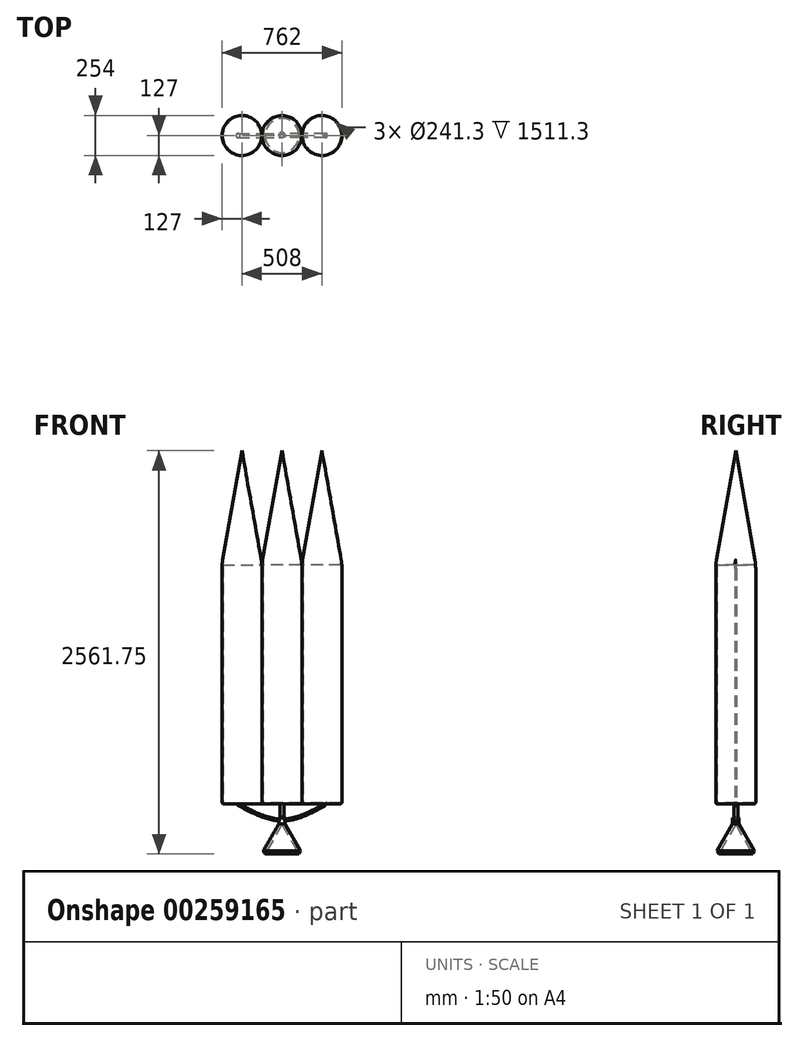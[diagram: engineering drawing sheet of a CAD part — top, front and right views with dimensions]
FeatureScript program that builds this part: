
annotation { "Feature Type Name" : "Feature", "Feature Type Description" : "" }
export const myFeature = defineFeature(function(context is Context, id is Id, definition is map)
    precondition{}
    {
        {
            var Q0;
            Q0=qCreatedBy(makeId("Top.planeOp"),FACE);
            var sketch = newSketch(context, id + "F0", { "sketchPlane" : qUnion([Q0])});
            skCircle(sketch, "E0", {"center": v(0, 0) * mm, "radius": 127 * mm});
            skCircle(sketch, "E1", {"center": v(-127, 0) * mm, "radius": 127 * mm});
            skCircle(sketch, "E2", {"center": v(-254, 0) * mm, "radius": 127 * mm});
            skCircle(sketch, "E3", {"center": v(127, 0) * mm, "radius": 127 * mm});
            skCircle(sketch, "E4", {"center": v(254, 0) * mm, "radius": 127 * mm});
            skLineSegment(sketch, "E5.bottom", {"start": v(-276, 5.08) * mm, "end": v(273.28, 5.08) * mm});
            skLineSegment(sketch, "E5.top", {"start": v(-276, -5.08) * mm, "end": v(273.28, -5.08) * mm});
            skLineSegment(sketch, "E5.left", {"start": v(-276, 5.08) * mm, "end": v(-276, -5.08) * mm});
            skLineSegment(sketch, "E5.right", {"start": v(273.28, 5.08) * mm, "end": v(273.28, -5.08) * mm});
            skSolve(sketch);
        }
        {
            var Q0;
            {var subQ0=sQuery(id+"F0.wireOp",EDGE,"E3");var subQ1=sQuery(id+"F0.wireOp",EDGE,"E0");var subQ2=makeQuery(id+"F0.imprint","INTERSECT",VERTEX,{"disambiguationData":[OD(0.0)],"derivedFrom":[subQ1,subQ0]});Q0=makeQuery(id+"F0.imprint","IMPRINT",FACE,{"disambiguationData":[TD([[makeQuery(id+"F0.imprint","IMPRINT",EDGE,{"disambiguationData":[TD([[subQ2,1.0]])],"derivedFrom":subQ1}),1.0]])]});}
            var Q1;
            {var subQ0=sQuery(id+"F0.wireOp",EDGE,"E3");var subQ1=sQuery(id+"F0.wireOp",EDGE,"E0");var subQ2=makeQuery(id+"F0.imprint","INTERSECT",VERTEX,{"disambiguationData":[OD(0.0)],"derivedFrom":[subQ1,subQ0]});Q1=makeQuery(id+"F0.imprint","IMPRINT",FACE,{"disambiguationData":[TD([[makeQuery(id+"F0.imprint","IMPRINT",EDGE,{"disambiguationData":[TD([[subQ2,-1.0]])],"derivedFrom":subQ1}),1.0]])]});}
            var Q2;
            {var subQ0=sQuery(id+"F0.wireOp",EDGE,"E1");var subQ1=sQuery(id+"F0.wireOp",EDGE,"E0");var subQ2=makeQuery(id+"F0.imprint","INTERSECT",VERTEX,{"disambiguationData":[OD(0.0)],"derivedFrom":[subQ1,subQ0]});Q2=makeQuery(id+"F0.imprint","IMPRINT",FACE,{"disambiguationData":[TD([[makeQuery(id+"F0.imprint","IMPRINT",EDGE,{"disambiguationData":[TD([[subQ2,-1.0]])],"derivedFrom":subQ1}),1.0]])]});}
            var Q3;
            {var subQ0=sQuery(id+"F0.wireOp",EDGE,"E1");var subQ1=sQuery(id+"F0.wireOp",EDGE,"E0");var subQ2=makeQuery(id+"F0.imprint","INTERSECT",VERTEX,{"disambiguationData":[OD(1.0)],"derivedFrom":[subQ1,subQ0]});Q3=makeQuery(id+"F0.imprint","IMPRINT",FACE,{"disambiguationData":[TD([[makeQuery(id+"F0.imprint","IMPRINT",EDGE,{"disambiguationData":[TD([[subQ2,1.0]])],"derivedFrom":subQ1}),1.0]])]});}
            var Q4;
            {var subQ0=sQuery(id+"F0.wireOp",EDGE,"E1");var subQ1=sQuery(id+"F0.wireOp",EDGE,"E0");var subQ2=makeQuery(id+"F0.imprint","INTERSECT",VERTEX,{"disambiguationData":[OD(1.0)],"derivedFrom":[subQ1,subQ0]});Q4=makeQuery(id+"F0.imprint","IMPRINT",FACE,{"disambiguationData":[TD([[makeQuery(id+"F0.imprint","IMPRINT",EDGE,{"disambiguationData":[TD([[subQ2,-1.0]])],"derivedFrom":subQ1}),1.0]])]});}
            var Q5;
            {var subQ0=sQuery(id+"F0.wireOp",EDGE,"E3");var subQ1=sQuery(id+"F0.wireOp",EDGE,"E0");var subQ2=makeQuery(id+"F0.imprint","INTERSECT",VERTEX,{"disambiguationData":[OD(1.0)],"derivedFrom":[subQ1,subQ0]});Q5=makeQuery(id+"F0.imprint","IMPRINT",FACE,{"disambiguationData":[TD([[makeQuery(id+"F0.imprint","IMPRINT",EDGE,{"disambiguationData":[TD([[subQ2,-1.0]])],"derivedFrom":subQ1}),1.0]])]});}
            var Q6;
            {var subQ0=sQuery(id+"F0.wireOp",EDGE,"E5.left");Q6=makeQuery(id+"F0.imprint","IMPRINT",FACE,{"disambiguationData":[TD([[makeQuery(id+"F0.imprint","IMPRINT",EDGE,{"derivedFrom":subQ0}),-1.0]])]});}
            var Q7;
            {var subQ0=sQuery(id+"F0.wireOp",EDGE,"E2");var subQ1=sQuery(id+"F0.wireOp",EDGE,"E1");var subQ2=makeQuery(id+"F0.imprint","INTERSECT",VERTEX,{"disambiguationData":[OD(0.0)],"derivedFrom":[subQ1,subQ0]});Q7=makeQuery(id+"F0.imprint","IMPRINT",FACE,{"disambiguationData":[TD([[makeQuery(id+"F0.imprint","IMPRINT",EDGE,{"disambiguationData":[TD([[subQ2,-1.0]])],"derivedFrom":subQ1}),1.0]])]});}
            var Q8;
            {var subQ0=sQuery(id+"F0.wireOp",EDGE,"E2");var subQ1=sQuery(id+"F0.wireOp",EDGE,"E1");var subQ2=makeQuery(id+"F0.imprint","INTERSECT",VERTEX,{"disambiguationData":[OD(1.0)],"derivedFrom":[subQ1,subQ0]});Q8=makeQuery(id+"F0.imprint","IMPRINT",FACE,{"disambiguationData":[TD([[makeQuery(id+"F0.imprint","IMPRINT",EDGE,{"disambiguationData":[TD([[subQ2,1.0]])],"derivedFrom":subQ1}),1.0]])]});}
            var Q9;
            {var subQ8=sQuery(id+"F0.wireOp",EDGE,"E5.right");Q9=makeQuery(id+"F0.imprint","IMPRINT",FACE,{"disambiguationData":[TD([[makeQuery(id+"F0.imprint","IMPRINT",EDGE,{"derivedFrom":subQ8}),1.0]])]});}
            var Q10;
            {var subQ0=sQuery(id+"F0.wireOp",EDGE,"E4");var subQ1=sQuery(id+"F0.wireOp",EDGE,"E3");var subQ2=makeQuery(id+"F0.imprint","INTERSECT",VERTEX,{"disambiguationData":[OD(0.0)],"derivedFrom":[subQ1,subQ0]});Q10=makeQuery(id+"F0.imprint","IMPRINT",FACE,{"disambiguationData":[TD([[makeQuery(id+"F0.imprint","IMPRINT",EDGE,{"disambiguationData":[TD([[subQ2,1.0]])],"derivedFrom":subQ1}),1.0]])]});}
            var Q11;
            {var subQ0=sQuery(id+"F0.wireOp",EDGE,"E4");var subQ1=sQuery(id+"F0.wireOp",EDGE,"E3");var subQ2=makeQuery(id+"F0.imprint","INTERSECT",VERTEX,{"disambiguationData":[OD(1.0)],"derivedFrom":[subQ1,subQ0]});Q11=makeQuery(id+"F0.imprint","IMPRINT",FACE,{"disambiguationData":[TD([[makeQuery(id+"F0.imprint","IMPRINT",EDGE,{"disambiguationData":[TD([[subQ2,-1.0]])],"derivedFrom":subQ1}),1.0]])]});}
            var Q12;
            {var subQ0=sQuery(id+"F0.wireOp",EDGE,"E5.bottom");var subQ1=sQuery(id+"F0.wireOp",EDGE,"E1");var subQ2=makeQuery(id+"F0.imprint","INTERSECT",VERTEX,{"disambiguationData":[OD(1.0)],"derivedFrom":[subQ1,subQ0]});Q12=makeQuery(id+"F0.imprint","IMPRINT",FACE,{"disambiguationData":[TD([[makeQuery(id+"F0.imprint","IMPRINT",EDGE,{"disambiguationData":[TD([[subQ2,-1.0]])],"derivedFrom":subQ1}),1.0]])]});}
            var Q13;
            {var subQ4=sQuery(id+"F0.wireOp",EDGE,"E5.bottom");var subQ6=sQuery(id+"F0.wireOp",EDGE,"E0");var subQ7=makeQuery(id+"F0.imprint","INTERSECT",VERTEX,{"disambiguationData":[OD(1.0)],"derivedFrom":[subQ6,subQ4]});Q13=makeQuery(id+"F0.imprint","IMPRINT",FACE,{"disambiguationData":[TD([[makeQuery(id+"F0.imprint","IMPRINT",EDGE,{"disambiguationData":[TD([[subQ7,-1.0]])],"derivedFrom":subQ6}),1.0]])]});}
            var Q14;
            {var subQ5=sQuery(id+"F0.wireOp",EDGE,"E5.left");Q14=makeQuery(id+"F0.imprint","IMPRINT",FACE,{"disambiguationData":[TD([[makeQuery(id+"F0.imprint","IMPRINT",EDGE,{"derivedFrom":subQ5}),1.0]])]});}
            var Q15;
            {var subQ4=sQuery(id+"F0.wireOp",EDGE,"E0");var subQ6=sQuery(id+"F0.wireOp",EDGE,"E5.bottom");var subQ8=makeQuery(id+"F0.imprint","INTERSECT",VERTEX,{"disambiguationData":[OD(0.0)],"derivedFrom":[subQ4,subQ6]});Q15=makeQuery(id+"F0.imprint","IMPRINT",FACE,{"disambiguationData":[TD([[makeQuery(id+"F0.imprint","IMPRINT",EDGE,{"disambiguationData":[TD([[subQ8,1.0]])],"derivedFrom":subQ4}),1.0]])]});}
            var Q16;
            {var subQ0=sQuery(id+"F0.wireOp",EDGE,"E5.bottom");var subQ1=sQuery(id+"F0.wireOp",EDGE,"E3");var subQ2=makeQuery(id+"F0.imprint","INTERSECT",VERTEX,{"disambiguationData":[OD(0.0)],"derivedFrom":[subQ1,subQ0]});Q16=makeQuery(id+"F0.imprint","IMPRINT",FACE,{"disambiguationData":[TD([[makeQuery(id+"F0.imprint","IMPRINT",EDGE,{"disambiguationData":[TD([[subQ2,1.0]])],"derivedFrom":subQ1}),1.0]])]});}
            var Q17;
            {var subQ5=sQuery(id+"F0.wireOp",EDGE,"E5.right");Q17=makeQuery(id+"F0.imprint","IMPRINT",FACE,{"disambiguationData":[TD([[makeQuery(id+"F0.imprint","IMPRINT",EDGE,{"derivedFrom":subQ5}),-1.0]])]});}
            var Q18;
            {var subQ0=sQuery(id+"F0.wireOp",EDGE,"E5.bottom");var subQ1=sQuery(id+"F0.wireOp",EDGE,"E0");var subQ2=makeQuery(id+"F0.imprint","INTERSECT",VERTEX,{"disambiguationData":[OD(0.0)],"derivedFrom":[subQ1,subQ0]});Q18=makeQuery(id+"F0.imprint","IMPRINT",FACE,{"disambiguationData":[TD([[makeQuery(id+"F0.imprint","IMPRINT",EDGE,{"disambiguationData":[TD([[subQ2,1.0]])],"derivedFrom":subQ1}),-1.0]])]});}
            var Q19;
            {var subQ0=sQuery(id+"F0.wireOp",EDGE,"E4");var subQ1=sQuery(id+"F0.wireOp",EDGE,"E0");var subQ2=makeQuery(id+"F0.imprint","INTERSECT",VERTEX,{"derivedFrom":[subQ1,subQ0]});Q19=makeQuery(id+"F0.imprint","IMPRINT",FACE,{"disambiguationData":[TD([[makeQuery(id+"F0.imprint","IMPRINT",EDGE,{"disambiguationData":[TD([[subQ2,1.0]])],"derivedFrom":subQ1}),-1.0]])]});}
            var Q20;
            {var subQ0=sQuery(id+"F0.wireOp",EDGE,"E5.bottom");var subQ1=sQuery(id+"F0.wireOp",EDGE,"E0");var subQ2=makeQuery(id+"F0.imprint","INTERSECT",VERTEX,{"disambiguationData":[OD(1.0)],"derivedFrom":[subQ1,subQ0]});Q20=makeQuery(id+"F0.imprint","IMPRINT",FACE,{"disambiguationData":[TD([[makeQuery(id+"F0.imprint","IMPRINT",EDGE,{"disambiguationData":[TD([[subQ2,-1.0]])],"derivedFrom":subQ1}),-1.0]])]});}
            var Q21;
            {var subQ0=sQuery(id+"F0.wireOp",EDGE,"E2");var subQ1=sQuery(id+"F0.wireOp",EDGE,"E0");var subQ2=makeQuery(id+"F0.imprint","INTERSECT",VERTEX,{"derivedFrom":[subQ1,subQ0]});Q21=makeQuery(id+"F0.imprint","IMPRINT",FACE,{"disambiguationData":[TD([[makeQuery(id+"F0.imprint","IMPRINT",EDGE,{"disambiguationData":[TD([[subQ2,-1.0]])],"derivedFrom":subQ1}),-1.0]])]});}
            var Q22;
            {var subQ0=sQuery(id+"F0.wireOp",EDGE,"E3");var subQ1=sQuery(id+"F0.wireOp",EDGE,"E1");var subQ2=makeQuery(id+"F0.imprint","INTERSECT",VERTEX,{"derivedFrom":[subQ1,subQ0]});Q22=makeQuery(id+"F0.imprint","IMPRINT",FACE,{"disambiguationData":[TD([[makeQuery(id+"F0.imprint","IMPRINT",EDGE,{"disambiguationData":[TD([[subQ2,1.0]])],"derivedFrom":subQ1}),-1.0]])]});}
            var Q23;
            {var subQ0=sQuery(id+"F0.wireOp",EDGE,"E5.bottom");var subQ1=sQuery(id+"F0.wireOp",EDGE,"E1");var subQ2=makeQuery(id+"F0.imprint","INTERSECT",VERTEX,{"disambiguationData":[OD(0.0)],"derivedFrom":[subQ1,subQ0]});Q23=makeQuery(id+"F0.imprint","IMPRINT",FACE,{"disambiguationData":[TD([[makeQuery(id+"F0.imprint","IMPRINT",EDGE,{"disambiguationData":[TD([[subQ2,1.0]])],"derivedFrom":subQ1}),-1.0]])]});}
            extrude(context, id + "F1", {"entities" : qUnion([Q0, Q1, Q2, Q3, Q4, Q5, Q6, Q7, Q8, Q9, Q10, Q11, Q12, Q13, Q14, Q15, Q16, Q17, Q18, Q19, Q20, Q21, Q22, Q23]), "depth" : 1524 * mm});
        }
        {
            var Q0;
            Q0=makeQuery(id+"F1.opExtrude","CAP_FACE",FACE,{"disambiguationData":[OSD([sQuery(id+"F0.wireOp",EDGE,"E0"),sQuery(id+"F0.wireOp",EDGE,"E2"),sQuery(id+"F0.wireOp",EDGE,"E4"),sQuery(id+"F0.wireOp",EDGE,"E5.bottom"),sQuery(id+"F0.wireOp",EDGE,"E5.top")])],"isStart":false});
            var Q1;
            Q1=makeQuery(id+"F1.opExtrude","SWEPT_BODY",BODY,{"disambiguationData":[OSD([sQuery(id+"F0.wireOp",EDGE,"E0"),sQuery(id+"F0.wireOp",EDGE,"E2"),sQuery(id+"F0.wireOp",EDGE,"E4"),sQuery(id+"F0.wireOp",EDGE,"E5.bottom"),sQuery(id+"F0.wireOp",EDGE,"E5.top")])]});
            shell(context, id + "F2", {"isHollow" : true, "entities" : qUnion([Q0]), "parts" : qUnion([Q1]), "thickness" : 6.35 * mm});
        }
        {
            var Q0;
            Q0=qCreatedBy(makeId("Front.planeOp"),FACE);
            var sketch = newSketch(context, id + "F3", { "sketchPlane" : qUnion([Q0])});
            skFitSpline(sketch, "E6", {"points": [v(279.4, 0) * mm, v(0, -101.6) * mm, v(-279.4, 0) * mm], "startDerivative": vector(-647.7, -370.91) * mm, "endDerivative": vector(-647.7, 370.91) * mm});
            skSolve(sketch);
        }
        {
            var Q0;
            Q0=makeQuery(id+"F1.opExtrude","CAP_FACE",FACE,{"disambiguationData":[OSD([sQuery(id+"F0.wireOp",EDGE,"E0"),sQuery(id+"F0.wireOp",EDGE,"E2"),sQuery(id+"F0.wireOp",EDGE,"E4"),sQuery(id+"F0.wireOp",EDGE,"E5.bottom"),sQuery(id+"F0.wireOp",EDGE,"E5.top")])],"isStart":true});
            var sketch = newSketch(context, id + "F4", { "sketchPlane" : qUnion([Q0])});
            skCircle(sketch, "E7", {"center": v(-279.4, 0) * mm, "radius": 12.7 * mm});
            skSolve(sketch);
        }
        {
            var Q0;
            Q0=makeQuery(id+"F4.imprint","IMPRINT",FACE,{"disambiguationData":[TD([[makeQuery(id+"F4.imprint","IMPRINT",EDGE,{"derivedFrom":sQuery(id+"F4.wireOp",EDGE,"E7")}),1.0]])]});
            var Q1;
            Q1=sQuery(id+"F3.wireOp",EDGE,"E6");
            sweep(context, id + "F5", {"operationType" : NewBodyOperationType.ADD, "profiles" : qUnion([Q0]), "path" : qUnion([Q1])});
        }
        {
            var Q0;
            Q0=makeQuery(id+"F5.boolean.opBoolean","INTERSECT",EDGE,{"derivedFrom":[makeQuery(id+"F1.opExtrude","CAP_FACE",FACE,{"disambiguationData":[OSD([sQuery(id+"F0.wireOp",EDGE,"E0"),sQuery(id+"F0.wireOp",EDGE,"E2"),sQuery(id+"F0.wireOp",EDGE,"E4"),sQuery(id+"F0.wireOp",EDGE,"E5.bottom"),sQuery(id+"F0.wireOp",EDGE,"E5.top")])],"isStart":true}),makeQuery(id+"F5.opSweep","CAP_FACE",FACE,{"disambiguationData":[OSD([sQuery(id+"F3.wireOp",VERTEX,"E6.start"),sQuery(id+"F4.wireOp",EDGE,"E7")])],"isStart":false})]});
            fillet(context, id + "F6", {"entities" : qUnion([Q0]), "radius" : 12.7 * mm, "tangentPropagation" : true, "allowEdgeOverflow" : false});
        }
        {
            var Q0;
            Q0=makeQuery(id+"F1.opExtrude","CAP_FACE",FACE,{"disambiguationData":[OSD([sQuery(id+"F0.wireOp",EDGE,"E0"),sQuery(id+"F0.wireOp",EDGE,"E2"),sQuery(id+"F0.wireOp",EDGE,"E4"),sQuery(id+"F0.wireOp",EDGE,"E5.bottom"),sQuery(id+"F0.wireOp",EDGE,"E5.top")])],"isStart":true});
            var sketch = newSketch(context, id + "F7", { "sketchPlane" : qUnion([Q0])});
            skCircle(sketch, "E8", {"center": v(0, 0) * mm, "radius": 12.7 * mm});
            skSolve(sketch);
        }
        {
            var Q0;
            Q0 = qSketchRegion(id + "F7", true);
            var Q1;
            Q1=makeQuery(id+"F1.opExtrude","SWEPT_BODY",BODY,{"disambiguationData":[OSD([sQuery(id+"F0.wireOp",EDGE,"E0"),sQuery(id+"F0.wireOp",EDGE,"E2"),sQuery(id+"F0.wireOp",EDGE,"E4"),sQuery(id+"F0.wireOp",EDGE,"E5.bottom"),sQuery(id+"F0.wireOp",EDGE,"E5.top")])]});
            extrude(context, id + "F8", {"entities" : qUnion([Q0]), "operationType" : NewBodyOperationType.ADD, "endBoundEntityBody" : qUnion([Q1]), "depth" : 114.3 * mm});
        }
        {
            var Q0;
            Q0=makeQuery(id+"F8.opExtrude","CAP_FACE",FACE,{"disambiguationData":[OSD([sQuery(id+"F7.wireOp",EDGE,"E8")])],"isStart":false});
            extrude(context, id + "F9", {"entities" : qUnion([Q0]), "operationType" : NewBodyOperationType.ADD, "depth" : 203.2 * mm, "hasDraft" : true, "draftAngle" : 30 * degree, "hasSecondDirection" : true, "secondDirectionOppositeDirection" : true, "secondDirectionDepth" : 25.4 * mm, "hasSecondDirectionDraft" : true, "secondDirectionDraftAngle" : 15 * degree});
        }
        {
            var Q0;
            Q0=makeQuery(id+"F9.opExtrude","CAP_FACE",FACE,{"disambiguationData":[OSD([sQuery(id+"F7.wireOp",EDGE,"E8")])],"isStart":true});
            var Q1;
            Q1=makeQuery(id+"F9.*.split.splitOp","SPLIT",FACE,{"derivedFrom":makeQuery(id+"F9.opExtrude","SWEPT_FACE",FACE,{"disambiguationData":[OSD([sQuery(id+"F7.wireOp",EDGE,"E8")])]})});
            extrude(context, id + "F10", {"entities" : qUnion([Q0]), "operationType" : NewBodyOperationType.ADD, "endBound" : BoundingType.UP_TO_SURFACE, "oppositeDirection" : true, "endBoundEntityFace" : qUnion([Q1]), "depth" : 25.4 * mm});
        }
        {
            var Q0;
            {var subQ0=sQuery(id+"F7.wireOp",EDGE,"E8");var subQ1=makeQuery(id+"F8.opExtrude","SWEPT_FACE",FACE,{"disambiguationData":[OSD([subQ0])]});Q0=makeQuery(id+"F9.boolean.opBoolean","INTERSECT",EDGE,{"derivedFrom":[makeQuery(id+"F8.boolean.opBoolean","SPLIT",FACE,{"disambiguationData":[TD([makeQuery(id+"F1.opExtrude","CAP_FACE",FACE,{"disambiguationData":[OSD([sQuery(id+"F0.wireOp",EDGE,"E0"),sQuery(id+"F0.wireOp",EDGE,"E2"),sQuery(id+"F0.wireOp",EDGE,"E4"),sQuery(id+"F0.wireOp",EDGE,"E5.bottom"),sQuery(id+"F0.wireOp",EDGE,"E5.top")])],"isStart":true})])],"derivedFrom":subQ1}),makeQuery(id+"F9.opExtrude","CAP_FACE",FACE,{"disambiguationData":[OSD([subQ0])],"isStart":true})]});}
            chamfer(context, id + "F11", {"entities" : qUnion([Q0]), "width" : 6.35 * mm, "tangentPropagation" : true});
        }
        {
            var Q0;
            Q0=makeQuery(id+"F1.opExtrude","CAP_EDGE",EDGE,{"disambiguationData":[OSD([sQuery(id+"F0.wireOp",EDGE,"E2")])],"isStart":true});
            var Q1;
            Q1=makeQuery(id+"F1.opExtrude","CAP_EDGE",EDGE,{"disambiguationData":[OSD([sQuery(id+"F0.wireOp",EDGE,"E4")])],"isStart":true});
            var Q2;
            {var subQ0=sQuery(id+"F0.wireOp",EDGE,"E0");var subQ1=makeQuery(id+"F0.imprint","INTERSECT",VERTEX,{"disambiguationData":[OD(0.0)],"derivedFrom":[subQ0,sQuery(id+"F0.wireOp",EDGE,"E1")]});var subQ3=makeQuery(id+"F0.imprint","INTERSECT",VERTEX,{"disambiguationData":[OD(0.0)],"derivedFrom":[subQ0,sQuery(id+"F0.wireOp",EDGE,"E3")]});Q2=makeQuery(id+"F1.opExtrude","CAP_EDGE",EDGE,{"disambiguationData":[OSD([subQ0]),TDD([makeQuery(id+"F0.imprint","IMPRINT",EDGE,{"disambiguationData":[TD([[subQ3,1.0]])],"derivedFrom":subQ0}),makeQuery(id+"F0.imprint","IMPRINT",EDGE,{"disambiguationData":[TD([[subQ3,-1.0]])],"derivedFrom":subQ0}),makeQuery(id+"F0.imprint","IMPRINT",EDGE,{"disambiguationData":[TD([[subQ1,-1.0]])],"derivedFrom":subQ0})])],"isStart":true});}
            var Q3;
            {var subQ0=sQuery(id+"F0.wireOp",EDGE,"E0");var subQ1=makeQuery(id+"F0.imprint","INTERSECT",VERTEX,{"disambiguationData":[OD(1.0)],"derivedFrom":[subQ0,sQuery(id+"F0.wireOp",EDGE,"E3")]});var subQ3=makeQuery(id+"F0.imprint","INTERSECT",VERTEX,{"disambiguationData":[OD(1.0)],"derivedFrom":[subQ0,sQuery(id+"F0.wireOp",EDGE,"E1")]});Q3=makeQuery(id+"F1.opExtrude","CAP_EDGE",EDGE,{"disambiguationData":[OSD([subQ0]),TDD([makeQuery(id+"F0.imprint","IMPRINT",EDGE,{"disambiguationData":[TD([[subQ3,1.0]])],"derivedFrom":subQ0}),makeQuery(id+"F0.imprint","IMPRINT",EDGE,{"disambiguationData":[TD([[subQ3,-1.0]])],"derivedFrom":subQ0}),makeQuery(id+"F0.imprint","IMPRINT",EDGE,{"disambiguationData":[TD([[subQ1,-1.0]])],"derivedFrom":subQ0})])],"isStart":true});}
            fillet(context, id + "F12", {"entities" : qUnion([Q0, Q1, Q2, Q3]), "radius" : 12.7 * mm, "tangentPropagation" : true, "allowEdgeOverflow" : false});
        }
        {
            var Q0;
            Q0=makeQuery(id+"F9.opExtrude","CAP_FACE",FACE,{"disambiguationData":[OSD([sQuery(id+"F7.wireOp",EDGE,"E8")])],"isStart":false});
            chamfer(context, id + "F13", {"entities" : qUnion([Q0]), "width" : 12.7 * mm, "tangentPropagation" : true});
        }
        {
            var Q0;
            Q0=makeQuery(id+"F9.opExtrude","CAP_FACE",FACE,{"disambiguationData":[OSD([sQuery(id+"F7.wireOp",EDGE,"E8")])],"isStart":false});
            extrude(context, id + "F14", {"entities" : qUnion([Q0]), "operationType" : NewBodyOperationType.REMOVE, "oppositeDirection" : true, "depth" : 203.2 * mm, "hasDraft" : true, "draftAngle" : 30 * degree, "draftPullDirection" : true});
        }
        {
            var Q0;
            Q0=makeQuery(id+"F1.opExtrude","CAP_FACE",FACE,{"disambiguationData":[OSD([sQuery(id+"F0.wireOp",EDGE,"E0"),sQuery(id+"F0.wireOp",EDGE,"E2"),sQuery(id+"F0.wireOp",EDGE,"E4"),sQuery(id+"F0.wireOp",EDGE,"E5.bottom"),sQuery(id+"F0.wireOp",EDGE,"E5.top")])],"isStart":false});
            extrude(context, id + "F15", {"entities" : qUnion([Q0]), "operationType" : NewBodyOperationType.ADD, "depth" : 370.84 * mm, "hasDraft" : true, "draftAngle" : 10 * degree, "draftPullDirection" : true});
        }
        {
            var Q0;
            Q0=makeQuery(id+"F15.*.draft.opDraft","SPLIT",FACE,{"disambiguationData":[OD(1.0)],"derivedFrom":makeQuery(id+"F15.opExtrude","CAP_FACE",FACE,{"disambiguationData":[OSD([sQuery(id+"F0.wireOp",EDGE,"E0"),sQuery(id+"F0.wireOp",EDGE,"E2"),sQuery(id+"F0.wireOp",EDGE,"E4"),sQuery(id+"F0.wireOp",EDGE,"E5.bottom"),sQuery(id+"F0.wireOp",EDGE,"E5.top")])],"isStart":false})});
            var Q1;
            Q1=makeQuery(id+"F15.*.draft.opDraft","SPLIT",FACE,{"disambiguationData":[OD(0.0)],"derivedFrom":makeQuery(id+"F15.opExtrude","CAP_FACE",FACE,{"disambiguationData":[OSD([sQuery(id+"F0.wireOp",EDGE,"E0"),sQuery(id+"F0.wireOp",EDGE,"E2"),sQuery(id+"F0.wireOp",EDGE,"E4"),sQuery(id+"F0.wireOp",EDGE,"E5.bottom"),sQuery(id+"F0.wireOp",EDGE,"E5.top")])],"isStart":false})});
            var Q2;
            Q2=makeQuery(id+"F15.*.draft.opDraft","SPLIT",FACE,{"disambiguationData":[OD(2.0)],"derivedFrom":makeQuery(id+"F15.opExtrude","CAP_FACE",FACE,{"disambiguationData":[OSD([sQuery(id+"F0.wireOp",EDGE,"E0"),sQuery(id+"F0.wireOp",EDGE,"E2"),sQuery(id+"F0.wireOp",EDGE,"E4"),sQuery(id+"F0.wireOp",EDGE,"E5.bottom"),sQuery(id+"F0.wireOp",EDGE,"E5.top")])],"isStart":false})});
            extrude(context, id + "F16", {"entities" : qUnion([Q0, Q1, Q2]), "operationType" : NewBodyOperationType.ADD, "depth" : 381 * mm, "hasDraft" : true, "draftAngle" : 10 * degree, "draftPullDirection" : true});
        }
        {
            var Q0;
            {var subQ0=sQuery(id+"F0.wireOp",EDGE,"E4");Q0=makeQuery(id+"F15.boolean.opBoolean","MERGE",EDGE,{"derivedFrom":[makeQuery(id+"F1.opExtrude","CAP_EDGE",EDGE,{"disambiguationData":[OSD([subQ0])],"isStart":false}),makeQuery(id+"F15.opExtrude","CAP_EDGE",EDGE,{"disambiguationData":[OSD([subQ0])],"isStart":true})]});}
            var Q1;
            {var subQ0=sQuery(id+"F0.wireOp",EDGE,"E0");var subQ1=makeQuery(id+"F0.imprint","INTERSECT",VERTEX,{"disambiguationData":[OD(0.0)],"derivedFrom":[subQ0,sQuery(id+"F0.wireOp",EDGE,"E1")]});var subQ3=makeQuery(id+"F0.imprint","INTERSECT",VERTEX,{"disambiguationData":[OD(0.0)],"derivedFrom":[subQ0,sQuery(id+"F0.wireOp",EDGE,"E3")]});var subQ4=makeQuery(id+"F1.opExtrude","CAP_EDGE",EDGE,{"disambiguationData":[OSD([subQ0]),TDD([makeQuery(id+"F0.imprint","IMPRINT",EDGE,{"disambiguationData":[TD([[subQ3,1.0]])],"derivedFrom":subQ0}),makeQuery(id+"F0.imprint","IMPRINT",EDGE,{"disambiguationData":[TD([[subQ3,-1.0]])],"derivedFrom":subQ0}),makeQuery(id+"F0.imprint","IMPRINT",EDGE,{"disambiguationData":[TD([[subQ1,-1.0]])],"derivedFrom":subQ0})])],"isStart":false});Q1=makeQuery(id+"F15.boolean.opBoolean","MERGE",EDGE,{"derivedFrom":[subQ4,makeQuery(id+"F15.opExtrude","CAP_EDGE",EDGE,{"disambiguationData":[OSD([subQ0]),TDD([subQ4])],"isStart":true})]});}
            var Q2;
            {var subQ0=sQuery(id+"F0.wireOp",EDGE,"E2");Q2=makeQuery(id+"F15.boolean.opBoolean","MERGE",EDGE,{"derivedFrom":[makeQuery(id+"F1.opExtrude","CAP_EDGE",EDGE,{"disambiguationData":[OSD([subQ0])],"isStart":false}),makeQuery(id+"F15.opExtrude","CAP_EDGE",EDGE,{"disambiguationData":[OSD([subQ0])],"isStart":true})]});}
            var Q3;
            {var subQ0=sQuery(id+"F0.wireOp",EDGE,"E0");var subQ1=makeQuery(id+"F0.imprint","INTERSECT",VERTEX,{"disambiguationData":[OD(1.0)],"derivedFrom":[subQ0,sQuery(id+"F0.wireOp",EDGE,"E3")]});var subQ3=makeQuery(id+"F0.imprint","INTERSECT",VERTEX,{"disambiguationData":[OD(1.0)],"derivedFrom":[subQ0,sQuery(id+"F0.wireOp",EDGE,"E1")]});var subQ4=makeQuery(id+"F1.opExtrude","CAP_EDGE",EDGE,{"disambiguationData":[OSD([subQ0]),TDD([makeQuery(id+"F0.imprint","IMPRINT",EDGE,{"disambiguationData":[TD([[subQ3,1.0]])],"derivedFrom":subQ0}),makeQuery(id+"F0.imprint","IMPRINT",EDGE,{"disambiguationData":[TD([[subQ3,-1.0]])],"derivedFrom":subQ0}),makeQuery(id+"F0.imprint","IMPRINT",EDGE,{"disambiguationData":[TD([[subQ1,-1.0]])],"derivedFrom":subQ0})])],"isStart":false});Q3=makeQuery(id+"F15.boolean.opBoolean","MERGE",EDGE,{"derivedFrom":[subQ4,makeQuery(id+"F15.opExtrude","CAP_EDGE",EDGE,{"disambiguationData":[OSD([subQ0]),TDD([subQ4])],"isStart":true})]});}
            fillet(context, id + "F17", {"entities" : qUnion([Q0, Q1, Q2, Q3]), "radius" : 317.5 * mm, "tangentPropagation" : true, "allowEdgeOverflow" : false});
        }
    });
